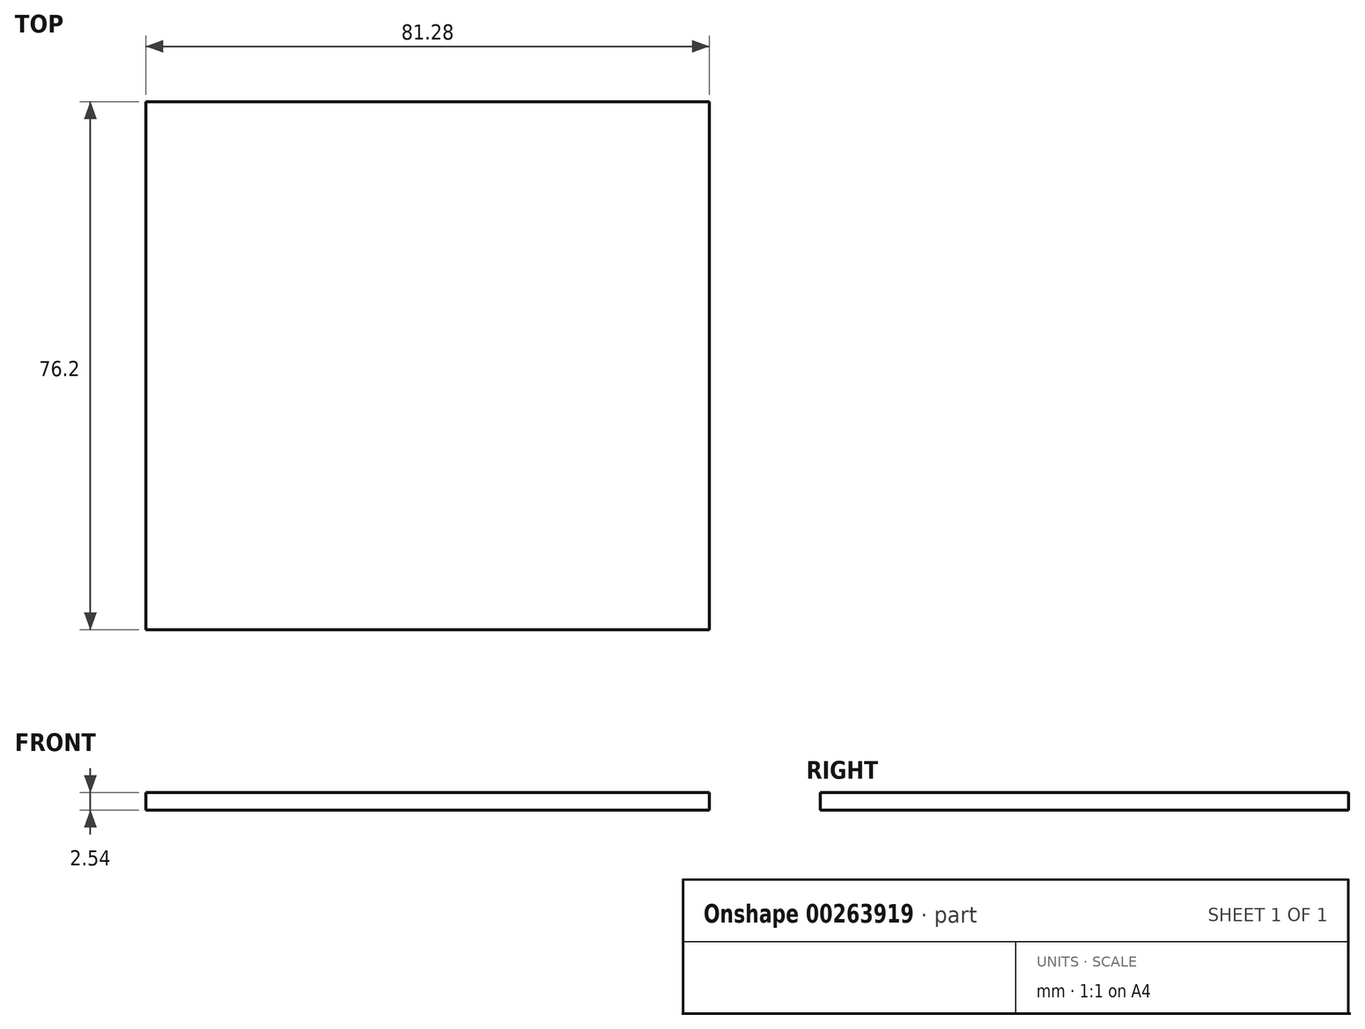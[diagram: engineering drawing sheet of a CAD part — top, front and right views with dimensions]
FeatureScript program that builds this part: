
annotation { "Feature Type Name" : "Feature", "Feature Type Description" : "" }
export const myFeature = defineFeature(function(context is Context, id is Id, definition is map)
    precondition{}
    {
        {
            var Q0;
            Q0=qCreatedBy(makeId("Front.planeOp"),FACE);
            var sketch = newSketch(context, id + "F0", { "sketchPlane" : qUnion([Q0])});
            skLineSegment(sketch, "E0.bottom", {"start": v(0, 0) * mm, "end": v(-81.28, 0) * mm});
            skLineSegment(sketch, "E0.top", {"start": v(0, -2.54) * mm, "end": v(-81.28, -2.54) * mm});
            skLineSegment(sketch, "E0.left", {"start": v(0, 0) * mm, "end": v(0, -2.54) * mm});
            skLineSegment(sketch, "E0.right", {"start": v(-81.28, 0) * mm, "end": v(-81.28, -2.54) * mm});
            skLineSegment(sketch, "E1.bottom", {"start": v(-81.28, 0) * mm, "end": v(-83.82, 0) * mm});
            skLineSegment(sketch, "E1.top", {"start": v(-81.28, -5.08) * mm, "end": v(-83.82, -5.08) * mm});
            skLineSegment(sketch, "E1.left", {"start": v(-81.28, 0) * mm, "end": v(-81.28, -5.08) * mm});
            skLineSegment(sketch, "E1.right", {"start": v(-83.82, 0) * mm, "end": v(-83.82, -5.08) * mm});
            skLineSegment(sketch, "E2.bottom", {"start": v(0, 0) * mm, "end": v(2.54, 0) * mm});
            skLineSegment(sketch, "E2.top", {"start": v(0, -5.08) * mm, "end": v(2.54, -5.08) * mm});
            skLineSegment(sketch, "E2.left", {"start": v(0, 0) * mm, "end": v(0, -5.08) * mm});
            skLineSegment(sketch, "E2.right", {"start": v(2.54, 0) * mm, "end": v(2.54, -5.08) * mm});
            skSolve(sketch);
        }
        {
            var Q0;
            {var subQ0=sQuery(id+"F0.wireOp",EDGE,"E0.bottom");Q0=makeQuery(id+"F0.imprint","IMPRINT",FACE,{"disambiguationData":[TD([[makeQuery(id+"F0.imprint","IMPRINT",EDGE,{"derivedFrom":subQ0}),1.0]])]});}
            extrude(context, id + "F1", {"entities" : qUnion([Q0]), "depth" : 76.2 * mm});
        }
    });
